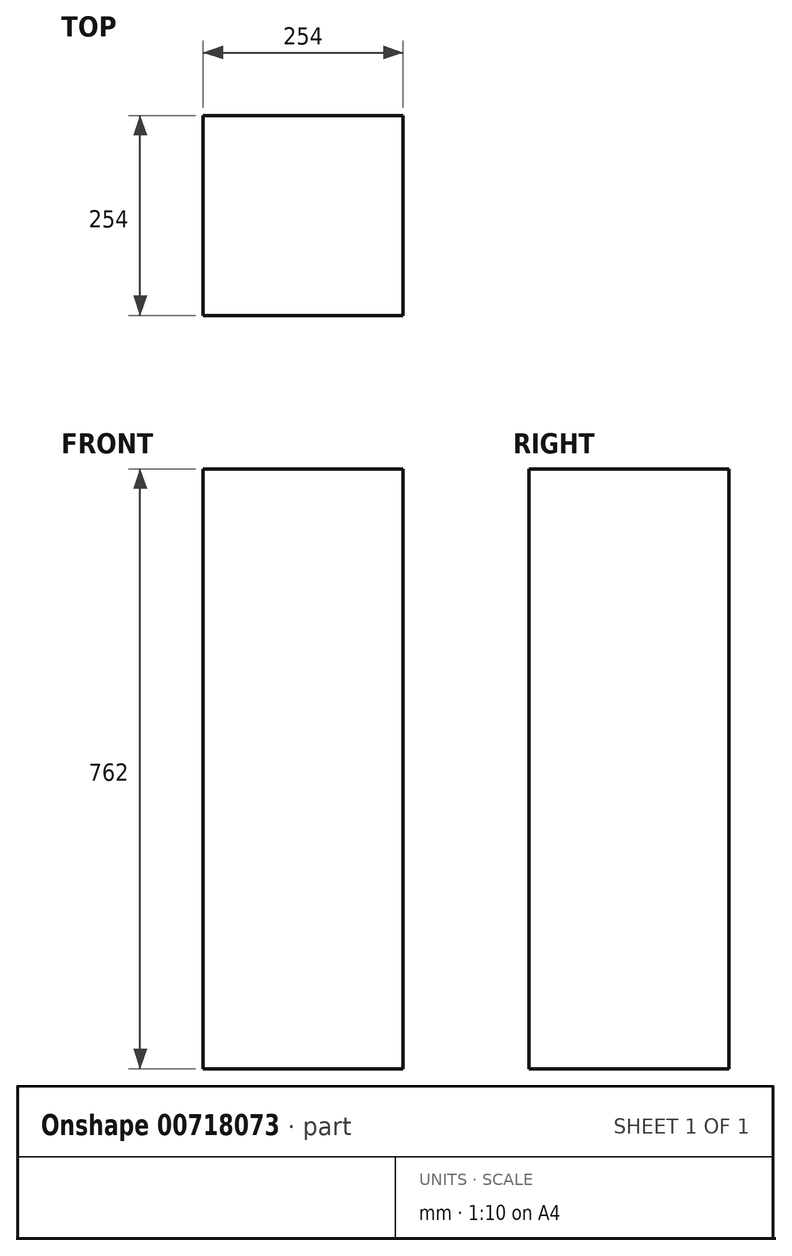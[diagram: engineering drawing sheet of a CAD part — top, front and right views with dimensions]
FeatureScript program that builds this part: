
annotation { "Feature Type Name" : "Feature", "Feature Type Description" : "" }
export const myFeature = defineFeature(function(context is Context, id is Id, definition is map)
    precondition{}
    {
        {
            var Q0;
            Q0=qCreatedBy(makeId("Front.planeOp"),FACE);
            var sketch = newSketch(context, id + "F0", { "sketchPlane" : qUnion([Q0])});
            skLineSegment(sketch, "E0.bottom", {"start": v(127, -381) * mm, "end": v(-127, -381) * mm});
            skLineSegment(sketch, "E0.top", {"start": v(127, 381) * mm, "end": v(-127, 381) * mm});
            skLineSegment(sketch, "E0.left", {"start": v(127, -381) * mm, "end": v(127, 381) * mm});
            skLineSegment(sketch, "E0.right", {"start": v(-127, -381) * mm, "end": v(-127, 381) * mm});
            skPoint(sketch, "E0.middle", {"position": v(0, 0) * mm});
            skSolve(sketch);
        }
        {
            var Q0;
            Q0 = qSketchRegion(id + "F0", true);
            extrude(context, id + "F1", {"entities" : qUnion([Q0]), "depth" : 254 * mm, "offsetDistance" : 25.4 * mm});
        }
    });
